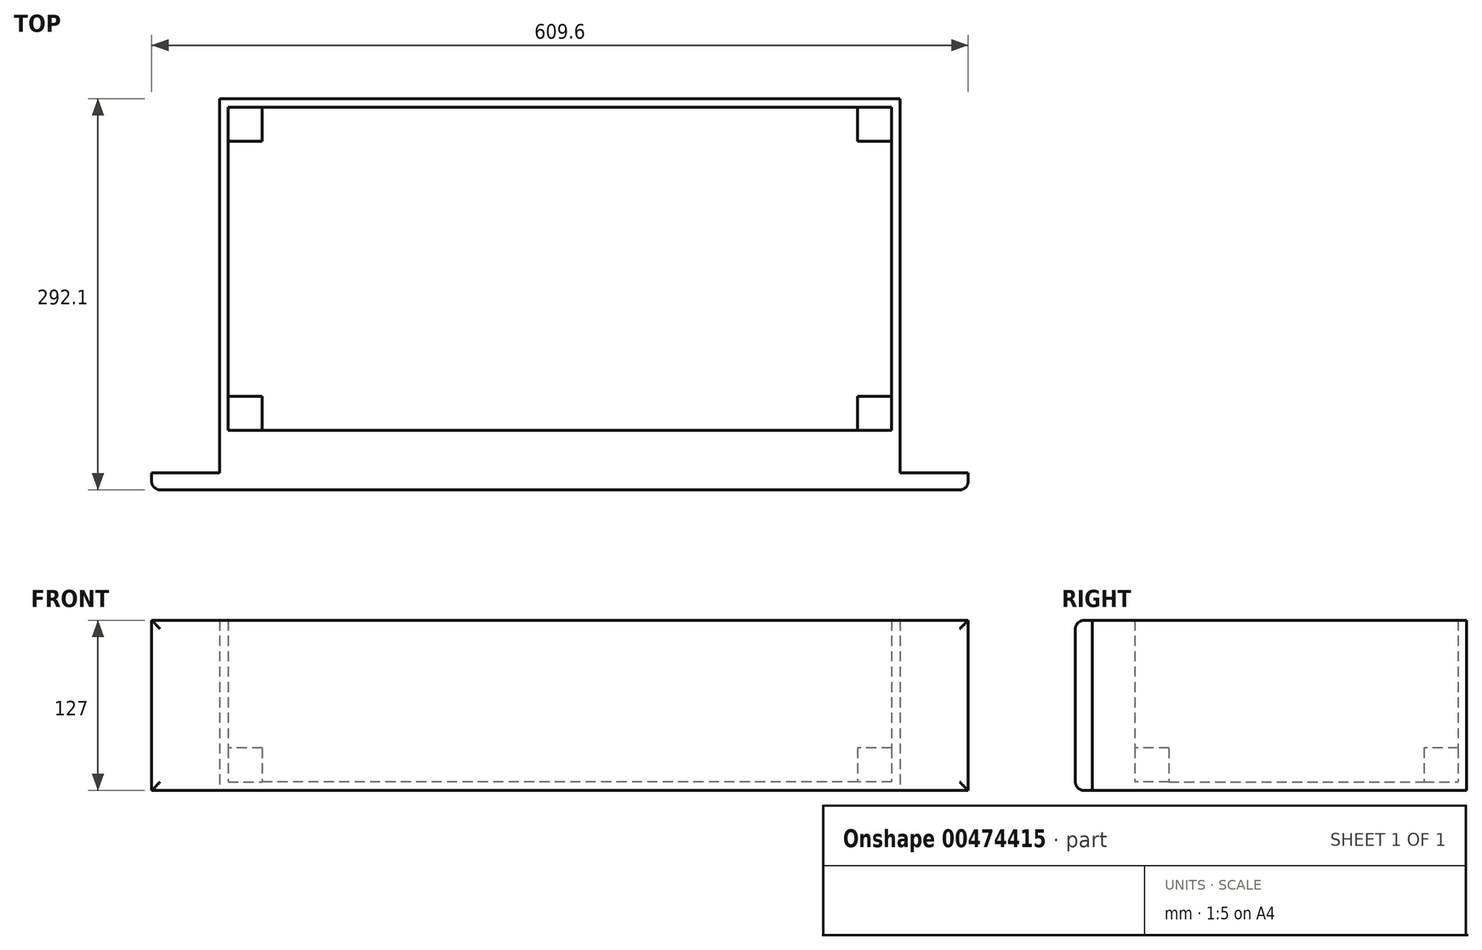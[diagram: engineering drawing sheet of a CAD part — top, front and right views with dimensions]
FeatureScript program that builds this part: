
annotation { "Feature Type Name" : "Feature", "Feature Type Description" : "" }
export const myFeature = defineFeature(function(context is Context, id is Id, definition is map)
    precondition{}
    {
        {
            var Q0;
            Q0=qCreatedBy(makeId("Top.planeOp"),FACE);
            var sketch = newSketch(context, id + "F0", { "sketchPlane" : qUnion([Q0])});
            skLineSegment(sketch, "E0.bottom", {"start": v(-254, -127) * mm, "end": v(254, -127) * mm});
            skLineSegment(sketch, "E0.top", {"start": v(-254, 127) * mm, "end": v(254, 127) * mm});
            skLineSegment(sketch, "E0.left", {"start": v(-254, -127) * mm, "end": v(-254, 127) * mm});
            skLineSegment(sketch, "E0.right", {"start": v(254, -127) * mm, "end": v(254, 127) * mm});
            skLineSegment(sketch, "E1.bottom", {"start": v(-254, 127) * mm, "end": v(-247.65, 127) * mm});
            skLineSegment(sketch, "E1.top", {"start": v(-254, -127) * mm, "end": v(-247.65, -127) * mm});
            skLineSegment(sketch, "E1.left", {"start": v(-254, 127) * mm, "end": v(-254, -127) * mm});
            skLineSegment(sketch, "E1.right", {"start": v(-247.65, 127) * mm, "end": v(-247.65, -127) * mm});
            skLineSegment(sketch, "E2.top", {"start": v(-254, -120.65) * mm, "end": v(254, -120.65) * mm});
            skLineSegment(sketch, "E2.left", {"start": v(-254, -127) * mm, "end": v(-254, -120.65) * mm});
            skLineSegment(sketch, "E2.right", {"start": v(254, -127) * mm, "end": v(254, -120.65) * mm});
            skLineSegment(sketch, "E3.bottom", {"start": v(254, -127) * mm, "end": v(247.65, -127) * mm});
            skLineSegment(sketch, "E3.top", {"start": v(254, 127) * mm, "end": v(247.65, 127) * mm});
            skLineSegment(sketch, "E3.right", {"start": v(247.65, -127) * mm, "end": v(247.65, 127) * mm});
            skLineSegment(sketch, "E4.bottom", {"start": v(254, 127) * mm, "end": v(-254, 127) * mm});
            skLineSegment(sketch, "E4.top", {"start": v(254, 120.65) * mm, "end": v(-254, 120.65) * mm});
            skLineSegment(sketch, "E4.left", {"start": v(254, 127) * mm, "end": v(254, 120.65) * mm});
            skLineSegment(sketch, "E4.right", {"start": v(-254, 127) * mm, "end": v(-254, 120.65) * mm});
            skSolve(sketch);
        }
        {
            var Q0;
            {var subQ0=sQuery(id+"F0.wireOp",EDGE,"E1.right");var subQ1=sQuery(id+"F0.wireOp",EDGE,"E0.top");var subQ2=makeQuery(id+"F0.imprint","INTERSECT",VERTEX,{"derivedFrom":[subQ1,subQ0]});Q0=makeQuery(id+"F0.imprint","IMPRINT",FACE,{"disambiguationData":[TD([[makeQuery(id+"F0.imprint","IMPRINT",EDGE,{"disambiguationData":[TD([[subQ2,1.0]])],"derivedFrom":subQ1}),-1.0]])]});}
            var Q1;
            {var subQ0=sQuery(id+"F0.wireOp",EDGE,"E1.right");var subQ1=sQuery(id+"F0.wireOp",EDGE,"E0.bottom");var subQ2=makeQuery(id+"F0.imprint","INTERSECT",VERTEX,{"derivedFrom":[subQ1,subQ0]});Q1=makeQuery(id+"F0.imprint","IMPRINT",FACE,{"disambiguationData":[TD([[makeQuery(id+"F0.imprint","IMPRINT",EDGE,{"disambiguationData":[TD([[subQ2,1.0]])],"derivedFrom":subQ1}),1.0]])]});}
            var Q2;
            {var subQ0=sQuery(id+"F0.wireOp",EDGE,"E0.right");var subQ1=sQuery(id+"F0.wireOp",EDGE,"E0.bottom");var subQ2=makeQuery(id+"F0.imprint","INTERSECT",VERTEX,{"derivedFrom":[subQ1,subQ0]});Q2=makeQuery(id+"F0.imprint","IMPRINT",FACE,{"disambiguationData":[TD([[makeQuery(id+"F0.imprint","IMPRINT",EDGE,{"disambiguationData":[TD([[subQ2,1.0]])],"derivedFrom":subQ1}),1.0]])]});}
            var Q3;
            {var subQ0=sQuery(id+"F0.wireOp",EDGE,"E3.right");var subQ1=sQuery(id+"F0.wireOp",EDGE,"E0.top");var subQ2=makeQuery(id+"F0.imprint","INTERSECT",VERTEX,{"derivedFrom":[subQ1,subQ0]});Q3=makeQuery(id+"F0.imprint","IMPRINT",FACE,{"disambiguationData":[TD([[makeQuery(id+"F0.imprint","IMPRINT",EDGE,{"disambiguationData":[TD([[subQ2,-1.0]])],"derivedFrom":subQ1}),-1.0]])]});}
            var Q4;
            {var subQ0=sQuery(id+"F0.wireOp",EDGE,"E1.right");var subQ1=sQuery(id+"F0.wireOp",EDGE,"E0.top");var subQ2=makeQuery(id+"F0.imprint","INTERSECT",VERTEX,{"derivedFrom":[subQ1,subQ0]});Q4=makeQuery(id+"F0.imprint","IMPRINT",FACE,{"disambiguationData":[TD([[makeQuery(id+"F0.imprint","IMPRINT",EDGE,{"disambiguationData":[TD([[subQ2,-1.0]])],"derivedFrom":subQ1}),-1.0]])]});}
            var Q5;
            {var subQ0=sQuery(id+"F0.wireOp",EDGE,"E1.right");var subQ1=sQuery(id+"F0.wireOp",EDGE,"E0.bottom");var subQ2=makeQuery(id+"F0.imprint","INTERSECT",VERTEX,{"derivedFrom":[subQ1,subQ0]});Q5=makeQuery(id+"F0.imprint","IMPRINT",FACE,{"disambiguationData":[TD([[makeQuery(id+"F0.imprint","IMPRINT",EDGE,{"disambiguationData":[TD([[subQ2,-1.0]])],"derivedFrom":subQ1}),1.0]])]});}
            var Q6;
            {var subQ0=sQuery(id+"F0.wireOp",EDGE,"E2.top");var subQ1=sQuery(id+"F0.wireOp",EDGE,"E0.right");var subQ2=makeQuery(id+"F0.imprint","INTERSECT",VERTEX,{"derivedFrom":[subQ1,subQ0]});Q6=makeQuery(id+"F0.imprint","IMPRINT",FACE,{"disambiguationData":[TD([[makeQuery(id+"F0.imprint","IMPRINT",EDGE,{"disambiguationData":[TD([[subQ2,-1.0]])],"derivedFrom":subQ1}),1.0]])]});}
            var Q7;
            {var subQ0=sQuery(id+"F0.wireOp",EDGE,"E2.top");var subQ1=sQuery(id+"F0.wireOp",EDGE,"E0.left");var subQ2=makeQuery(id+"F0.imprint","INTERSECT",VERTEX,{"derivedFrom":[subQ1,subQ0]});Q7=makeQuery(id+"F0.imprint","IMPRINT",FACE,{"disambiguationData":[TD([[makeQuery(id+"F0.imprint","IMPRINT",EDGE,{"disambiguationData":[TD([[subQ2,-1.0]])],"derivedFrom":subQ1}),-1.0]])]});}
            extrude(context, id + "F1", {"entities" : qUnion([Q0, Q1, Q2, Q3, Q4, Q5, Q6, Q7]), "depth" : 127 * mm, "offsetDistance" : 25.4 * mm});
        }
        {
            var Q0;
            {var subQ0=sQuery(id+"F0.wireOp",EDGE,"E4.top");var subQ1=sQuery(id+"F0.wireOp",EDGE,"E1.right");var subQ2=makeQuery(id+"F0.imprint","INTERSECT",VERTEX,{"derivedFrom":[subQ1,subQ0]});Q0=makeQuery(id+"F0.imprint","IMPRINT",FACE,{"disambiguationData":[TD([[makeQuery(id+"F0.imprint","IMPRINT",EDGE,{"disambiguationData":[TD([[subQ2,-1.0]])],"derivedFrom":subQ1}),1.0]])]});}
            extrude(context, id + "F2", {"entities" : qUnion([Q0]), "operationType" : NewBodyOperationType.ADD, "depth" : 6.35 * mm, "offsetDistance" : 25.4 * mm});
        }
        {
            var Q0;
            Q0=makeQuery(id+"F2.opExtrude","CAP_FACE",FACE,{"disambiguationData":[OSD([sQuery(id+"F0.wireOp",EDGE,"E1.right"),sQuery(id+"F0.wireOp",EDGE,"E2.top"),sQuery(id+"F0.wireOp",EDGE,"E3.right"),sQuery(id+"F0.wireOp",EDGE,"E4.top")])],"isStart":false});
            var sketch = newSketch(context, id + "F3", { "sketchPlane" : qUnion([Q0])});
            skLineSegment(sketch, "E5.bottom", {"start": v(-247.65, 95.25) * mm, "end": v(-222.25, 95.25) * mm});
            skLineSegment(sketch, "E5.top", {"start": v(-247.65, 120.65) * mm, "end": v(-222.25, 120.65) * mm});
            skLineSegment(sketch, "E5.left", {"start": v(-247.65, 95.25) * mm, "end": v(-247.65, 120.65) * mm});
            skLineSegment(sketch, "E5.right", {"start": v(-222.25, 95.25) * mm, "end": v(-222.25, 120.65) * mm});
            skLineSegment(sketch, "E6.MirrorCS", {"start": v(-222.25, -95.25) * mm, "end": v(-222.25, -120.65) * mm});
            skLineSegment(sketch, "E7.MirrorCS", {"start": v(-247.65, -95.25) * mm, "end": v(-222.25, -95.25) * mm});
            skLineSegment(sketch, "E8.MirrorCS", {"start": v(222.25, 95.25) * mm, "end": v(222.25, 120.65) * mm});
            skLineSegment(sketch, "E9.MirrorCS", {"start": v(247.65, -95.25) * mm, "end": v(222.25, -95.25) * mm});
            skLineSegment(sketch, "E10.MirrorCS", {"start": v(222.25, -95.25) * mm, "end": v(222.25, -120.65) * mm});
            skLineSegment(sketch, "E11.MirrorCS", {"start": v(247.65, 95.25) * mm, "end": v(222.25, 95.25) * mm});
            skSolve(sketch);
        }
        {
            var Q0;
            {var subQ0=sQuery(id+"F3.wireOp",EDGE,"E6.MirrorCS");Q0=makeQuery(id+"F3.imprint","IMPRINT",FACE,{"disambiguationData":[TD([[makeQuery(id+"F3.imprint","IMPRINT",EDGE,{"derivedFrom":subQ0}),-1.0]])]});}
            var Q1;
            Q1=makeQuery(id+"F3.imprint","IMPRINT",FACE,{"disambiguationData":[TD([[makeQuery(id+"F3.imprint","IMPRINT",EDGE,{"derivedFrom":sQuery(id+"F3.wireOp",EDGE,"E5.bottom")}),1.0]])]});
            var Q2;
            {var subQ0=sQuery(id+"F3.wireOp",EDGE,"E8.MirrorCS");Q2=makeQuery(id+"F3.imprint","IMPRINT",FACE,{"disambiguationData":[TD([[makeQuery(id+"F3.imprint","IMPRINT",EDGE,{"derivedFrom":subQ0}),-1.0]])]});}
            var Q3;
            {var subQ0=sQuery(id+"F3.wireOp",EDGE,"E9.MirrorCS");Q3=makeQuery(id+"F3.imprint","IMPRINT",FACE,{"disambiguationData":[TD([[makeQuery(id+"F3.imprint","IMPRINT",EDGE,{"derivedFrom":subQ0}),1.0]])]});}
            extrude(context, id + "F4", {"entities" : qUnion([Q0, Q1, Q2, Q3]), "operationType" : NewBodyOperationType.ADD, "depth" : 25.4 * mm, "offsetDistance" : 25.4 * mm});
        }
        {
            var Q0;
            Q0=makeQuery(id+"F1.opExtrude","SWEPT_FACE",FACE,{"disambiguationData":[OSD([sQuery(id+"F0.wireOp",EDGE,"E0.bottom")])]});
            var sketch = newSketch(context, id + "F5", { "sketchPlane" : qUnion([Q0])});
            skLineSegment(sketch, "E12.bottom", {"start": v(-254, 0) * mm, "end": v(254, 0) * mm});
            skLineSegment(sketch, "E12.top", {"start": v(-254, 127) * mm, "end": v(254, 127) * mm});
            skLineSegment(sketch, "E12.left", {"start": v(-254, 0) * mm, "end": v(-254, 127) * mm});
            skLineSegment(sketch, "E12.right", {"start": v(254, 0) * mm, "end": v(254, 127) * mm});
            skSolve(sketch);
        }
        {
            var Q0;
            Q0 = qSketchRegion(id + "F5", true);
            extrude(context, id + "F6", {"entities" : qUnion([Q0]), "operationType" : NewBodyOperationType.ADD, "depth" : 25.4 * mm, "offsetDistance" : 25.4 * mm});
        }
        {
            var Q0;
            Q0=makeQuery(id+"F6.opExtrude","CAP_FACE",FACE,{"disambiguationData":[OSD([sQuery(id+"F5.wireOp",EDGE,"E12.bottom"),sQuery(id+"F5.wireOp",EDGE,"E12.top"),sQuery(id+"F5.wireOp",EDGE,"E12.left"),sQuery(id+"F5.wireOp",EDGE,"E12.right")])],"isStart":false});
            var sketch = newSketch(context, id + "F7", { "sketchPlane" : qUnion([Q0])});
            skLineSegment(sketch, "E13.bottom", {"start": v(-304.8, 0) * mm, "end": v(304.8, 0) * mm});
            skLineSegment(sketch, "E13.top", {"start": v(-304.8, 127) * mm, "end": v(304.8, 127) * mm});
            skLineSegment(sketch, "E13.left", {"start": v(-304.8, 0) * mm, "end": v(-304.8, 127) * mm});
            skLineSegment(sketch, "E13.right", {"start": v(304.8, 0) * mm, "end": v(304.8, 127) * mm});
            skSolve(sketch);
        }
        {
            var Q0;
            Q0 = qSketchRegion(id + "F7", true);
            extrude(context, id + "F8", {"entities" : qUnion([Q0]), "operationType" : NewBodyOperationType.ADD, "depth" : 12.7 * mm, "offsetDistance" : 25.4 * mm});
        }
        {
            var Q0;
            Q0=makeQuery(id+"F8.opExtrude","CAP_EDGE",EDGE,{"disambiguationData":[OSD([sQuery(id+"F7.wireOp",EDGE,"E13.left")])],"isStart":false});
            var Q1;
            Q1=makeQuery(id+"F8.opExtrude","CAP_EDGE",EDGE,{"disambiguationData":[OSD([sQuery(id+"F7.wireOp",EDGE,"E13.bottom")])],"isStart":false});
            var Q2;
            Q2=makeQuery(id+"F8.opExtrude","CAP_EDGE",EDGE,{"disambiguationData":[OSD([sQuery(id+"F7.wireOp",EDGE,"E13.right")])],"isStart":false});
            var Q3;
            Q3=makeQuery(id+"F8.opExtrude","CAP_EDGE",EDGE,{"disambiguationData":[OSD([sQuery(id+"F7.wireOp",EDGE,"E13.top")])],"isStart":false});
            fillet(context, id + "F9", {"entities" : qUnion([Q0, Q1, Q2, Q3]), "radius" : 6.35 * mm, "tangentPropagation" : true, "allowEdgeOverflow" : false});
        }
    });
